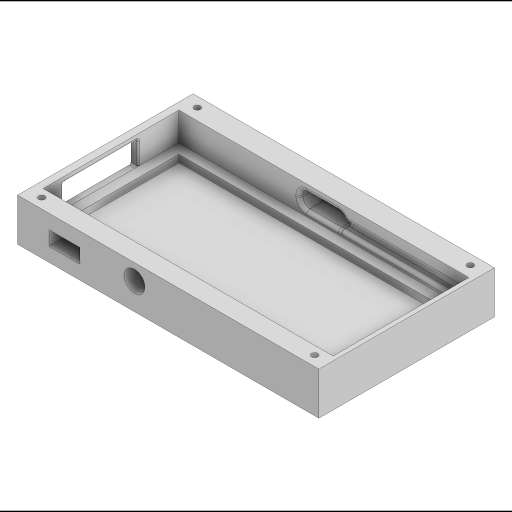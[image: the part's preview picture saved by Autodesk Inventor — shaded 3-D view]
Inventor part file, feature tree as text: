
AUTODESK INVENTOR PART (.ipt)
format: ipt  version: 2023 (Build 270158000, 158)  size: 673,280 bytes
history: native  units: in
note: dims shown in document units (in); Inventor stores cm internally (conversion verified against a paired STEP export)
features: extrude x14, sketch x14, projected_geometry x7, fillet x6, plane x1
ambient origin geometry x8: Origin, YZ Plane, XZ Plane, XY Plane, X Axis, Y Axis, Z Axis, Center Point
bodies: Solid1 (feature_tree)
feature tree (42):
  extrude  "Extrusion1"  Depth=4.6875in
  extrude  "Extrusion2"  Depth=1.25in TaperAngle=0.0deg
  extrude  "Circuit Board Ledge"  Depth=0.35in
  extrude  "Arduino Opening"  Depth=1.0in TaperAngle=0.0deg
  extrude  "Contrast Pot Access"  Depth=0.85in
  extrude  "Load Cell & Motor Wire Exit"  Depth=0.185in
  extrude  "Power Wire & i2c multi out"  Depth=0.5in
  fillet  "Fillet1"  Radius=0.5625in
  fillet  "Fillet2"  Radius=4.125in
  plane  "Work Plane1"
  fillet  "Fillet6"  Radius=1.125in
  fillet  "Fillet7"  Radius=0.5in
  extrude  "Cable Track"  Depth=0.5in
  extrude  "Extrusion16"  Depth=4.5in
  extrude  "Extrusion17"  Depth=1.0in TaperAngle=0.0deg
  extrude  "Extrusion18"  Depth=0.125in
  extrude  "Extrusion19"  Depth=0.0625in
  extrude  "Extrusion20"  Depth=0.2in
  fillet  "Fillet12"  Radius=4.15in
  fillet  "Fillet13"  Radius=0.25in
  extrude  "Extrusion21"  Depth=0.5in TaperAngle=0.0deg
  sketch  "Sketch1"  dims[d0=10.125in d1=4.6875in]
  sketch  "Sketch2"  dims[d2=0.25in d3=1.25in d4=0.0in]
  projected_geometry  "Projected Loop1"
  sketch  "Sketch3"  dims[d5=0.25in d6=0.0in d7=0.35in]
  projected_geometry  "Projected Loop2"
  sketch  "Sketch4"  dims[d8=0.25in d9=0.0in d10=1.0in d11=0.0in]
  sketch  "Sketch5"  dims[d12=2.65in d13=0.85in]
  sketch  "Sketch6"  dims[d14=0.45in d15=0.185in]
  sketch  "Sketch7"  dims[d16=1.0in d17=0.0in d18=0.7289in d19=0.5625in d20=4.125in d21=1.125in d22=0.5in]
  sketch  "Sketch12"  dims[d23=0.5in d24=2.2in]
  sketch  "Sketch18"  dims[d25=1.0in d26=0.0in d27=4.5in]
  projected_geometry  "Projected Loop6"
  sketch  "Sketch19"  dims[d28=4.5in d29=1.0in d30=0.0in]
  projected_geometry  "Projected Loop7"
  sketch  "Sketch20"  dims[d31=0.25in d32=0.125in]
  projected_geometry  "Projected Loop8"
  sketch  "Sketch21"  dims[d33=-0.625in d59=0.0625in d60=0.0625in]
  projected_geometry  "Projected Loop9"
  sketch  "Sketch22"  dims[d61=0.465in d62=0.2in d63=4.15in d64=0.25in]
  projected_geometry  "Projected Loop10"
  sketch  "Sketch23"  dims[d65=0.25in d66=0.0in d113=0.5in d114=0.0in d115=0.5in d116=0.0in d117=0.1in d118=0.0in d119=0.1in d120=0.0in d121=0.25in d122=0.0in d123=0.125in d124=0.125in d125=0.217in d126=0.35in d127=0.5in d128=0.5in d129=0.35in d130=0.217in d131=0.35in d132=0.217in d133=0.217in d134=0.35in d135=0.5in d136=0.5in d137=0.375in d138=0.0in]
